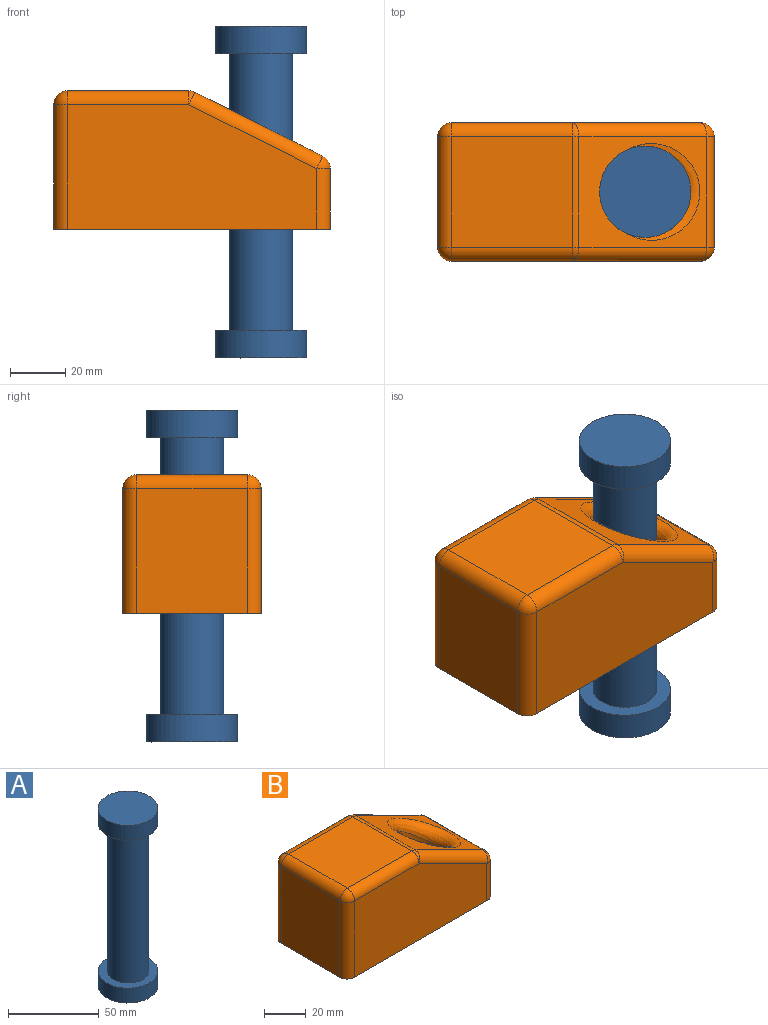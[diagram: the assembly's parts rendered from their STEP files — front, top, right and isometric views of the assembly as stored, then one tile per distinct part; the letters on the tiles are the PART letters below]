
ASSEMBLY  parts=2 mates=1
PART A: 7 faces, bbox 33x33x120 mm
  f0: cylinder r=11.5mm len=100mm, axis (0,0,-1), area 7225.7mm2, adj f3,f6
  f1: cylinder r=16.5mm len=33mm, axis (0,0,-1), area 1036.7mm2, adj f2,f3
  f2: plane 33x33mm, normal (0,0,1), area 855.3mm2, adj f1
  f3: plane 33x33mm, normal (0,0,-1), area 439.8mm2, adj f0,f1
  f4: cylinder r=16.5mm len=33mm, axis (0,0,1), area 1036.7mm2, adj f5,f6
  f5: plane 33x33mm, normal (0,0,-1), area 855.3mm2, adj f4
  f6: plane 33x33mm, normal (0,0,1), area 439.8mm2, adj f0,f4
PART B: 52 faces, bbox 100x50x50 mm
  f0: plane 29x29mm, normal (0,0,-1), area 169.6mm2, adj f8,f33
  f1: plane 43.82x40mm, normal (0,0,1), area 1752.8mm2, adj f17,f20,f23,f26
  f2: plane 45x40mm, normal (-1,0,0), area 1800mm2, adj f3,f21,f22,f26
  f3: plane 100x50mm, normal (0,0,-1), area 570.3mm2, adj f2,f4,f6,f7,f10,f11,f21,f22
  f4: plane 40x21.91mm, normal (1,0,0), area 876.4mm2, adj f3,f10,f11,f12
  f5: plane 46.18x40mm, normal (0.45,0,0.89), area 989.6mm2, adj f9,f12,f15,f16,f17
  f6: plane 90x45mm, normal (0,-1,0), area 3516.8mm2, adj f3,f10,f15,f20,f21
  f7: plane 90x45mm, normal (0,1,0), area 3516.8mm2, adj f3,f11,f16,f22,f23
  f8: cylinder r=12.5mm len=40.66mm, axis (0,0,1), area 2506.2mm2, adj f0,f9
  f9: bspline ~34.98x34.96mm, area 757.8mm2, adj f5,f8
  f10: cylinder r=5mm len=21.91mm, axis (0,0,-1), area 172.1mm2, adj f3,f4,f6,f13
  f11: cylinder r=5mm len=21.91mm, axis (0,0,1), area 172.1mm2, adj f3,f4,f7,f14
  f12: cylinder r=5mm len=40mm, axis (0,1,0), area 221.4mm2, adj f4,f5,f13,f14
  f13: sphere r=5mm, area 19.6mm2, adj f10,f12,f15
  f14: sphere r=5mm, area 19.6mm2, adj f11,f12,f16
  f15: cylinder r=5mm len=48.42mm, axis (0.89,0,-0.45), area 405.5mm2, adj f5,f6,f13,f18
  f16: cylinder r=5mm len=48.42mm, axis (-0.89,0,0.45), area 405.5mm2, adj f5,f7,f14,f19
  f17: cylinder r=5mm len=40mm, axis (0,1,0), area 92.7mm2, adj f1,f5,f18,f19
  f18: sphere r=5mm, area 11.6mm2, adj f15,f17,f20
  f19: sphere r=5mm, area 11.6mm2, adj f16,f17,f23
  f20: cylinder r=5mm len=43.82mm, axis (1,0,0), area 344.2mm2, adj f1,f6,f18,f24
  f21: cylinder r=5mm len=45mm, axis (0,0,1), area 353.4mm2, adj f2,f3,f6,f24
  f22: cylinder r=5mm len=45mm, axis (0,0,-1), area 353.4mm2, adj f2,f3,f7,f25
  f23: cylinder r=5mm len=43.82mm, axis (-1,0,0), area 344.2mm2, adj f1,f7,f19,f25
  f24: sphere r=5mm, area 39.3mm2, adj f20,f21,f26
  f25: sphere r=5mm, area 39.3mm2, adj f22,f23,f26
  f26: cylinder r=5mm len=40mm, axis (0,1,0), area 314.2mm2, adj f1,f2,f24,f25
  f27: plane 43.82x40mm, normal (0,0,-1), area 1752.8mm2, adj f42,f45,f48,f51
  f28: plane 45x40mm, normal (1,0,0), area 1800mm2, adj f3,f46,f47,f51
  f29: plane 40x21.91mm, normal (-1,0,0), area 876.4mm2, adj f3,f35,f36,f37
  f30: plane 46.18x40mm, normal (-0.45,0,-0.89), area 989.6mm2, adj f34,f37,f40,f41,f42
  f31: plane 90x45mm, normal (0,1,0), area 3516.8mm2, adj f3,f35,f40,f45,f46
  f32: plane 90x45mm, normal (0,-1,0), area 3516.8mm2, adj f3,f36,f41,f47,f48
  f33: cylinder r=14.5mm len=40.66mm, axis (0,0,1), area 2907.2mm2, adj f0,f34
  f34: bspline ~34.98x34.96mm, area 492.3mm2, adj f30,f33
  f35: cylinder r=3mm len=21.91mm, axis (0,0,-1), area 103.2mm2, adj f3,f29,f31,f38
  f36: cylinder r=3mm len=21.91mm, axis (0,0,1), area 103.2mm2, adj f3,f29,f32,f39
  f37: cylinder r=3mm len=40mm, axis (0,1,0), area 132.9mm2, adj f29,f30,f38,f39
  f38: sphere r=3mm, area 7.1mm2, adj f35,f37,f40
  f39: sphere r=3mm, area 7.1mm2, adj f36,f37,f41
  f40: cylinder r=3mm len=47.52mm, axis (0.89,0,-0.45), area 243.3mm2, adj f30,f31,f38,f43
  f41: cylinder r=3mm len=47.52mm, axis (-0.89,0,0.45), area 243.3mm2, adj f30,f32,f39,f44
  f42: cylinder r=3mm len=40mm, axis (0,1,0), area 55.6mm2, adj f27,f30,f43,f44
  f43: sphere r=3mm, area 4.2mm2, adj f40,f42,f45
  f44: sphere r=3mm, area 4.2mm2, adj f41,f42,f48
  f45: cylinder r=3mm len=43.82mm, axis (1,0,0), area 206.5mm2, adj f27,f31,f43,f49
  f46: cylinder r=3mm len=45mm, axis (0,0,1), area 212.1mm2, adj f3,f28,f31,f49
  f47: cylinder r=3mm len=45mm, axis (0,0,-1), area 212.1mm2, adj f3,f28,f32,f50
  f48: cylinder r=3mm len=43.82mm, axis (-1,0,0), area 206.5mm2, adj f27,f32,f44,f50
  f49: sphere r=3mm, area 14.1mm2, adj f45,f46,f51
  f50: sphere r=3mm, area 19.3mm2, adj f47,f48,f51
  f51: cylinder r=3mm len=40mm, axis (0,1,0), area 188.5mm2, adj f27,f28,f49,f50
PLACE A rot(axis=(-0.8,-0.44,0.42),0deg) t=(-9.81,5.38,-36.9)mm
PLACE B rot(axis=(-0.8,-0.44,0.42),0deg) t=(-9.81,5.38,-0.34)mm fixed
MATE slider A.f0 <-> B.f8  axis (0,0,-1) through (65.19,5.38,13.1)mm
